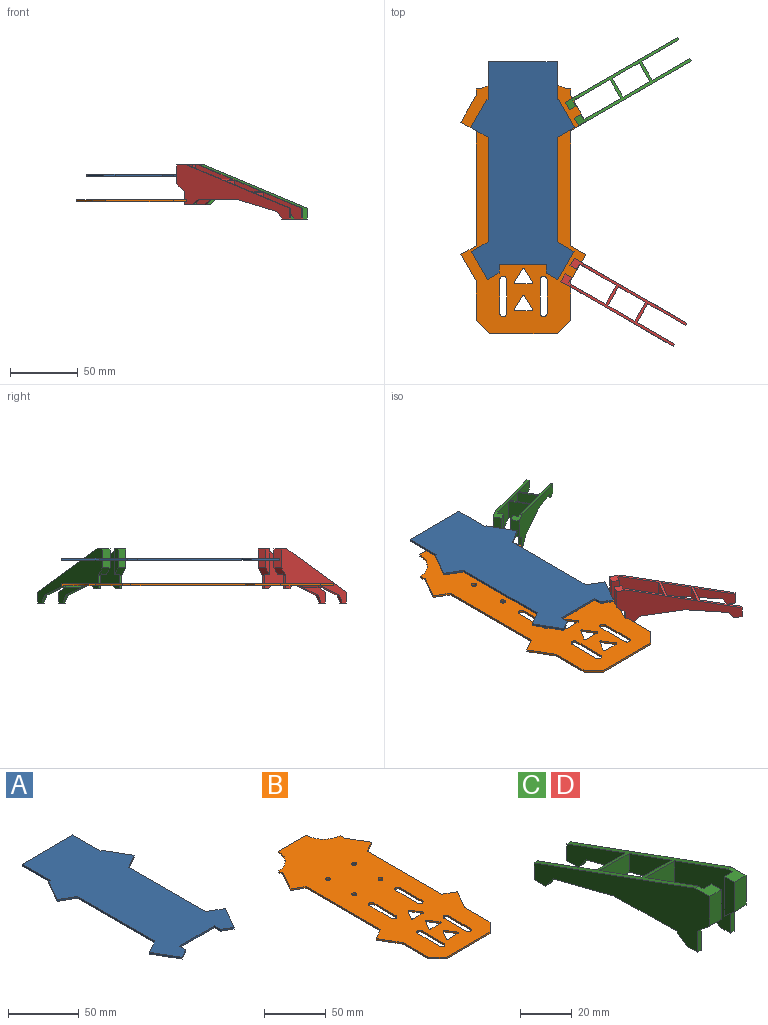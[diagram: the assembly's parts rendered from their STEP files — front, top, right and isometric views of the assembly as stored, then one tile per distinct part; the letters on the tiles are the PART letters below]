
ASSEMBLY  parts=4 mates=2
PART A: 22 faces, bbox 77x161.1x1.5 mm
  f0: plane 77.29x1.5mm, normal (-1,0,0), area 115.9mm2, adj f1,f19,f20,f21
  f1: plane 12.5x7.22mm, normal (-0.5,0.87,0), area 21.7mm2, adj f0,f2,f20,f21
  f2: plane 20.78x12mm, normal (-0.87,-0.5,0), area 36mm2, adj f1,f3,f20,f21
  f3: plane 8.5x4.91mm, normal (0.5,-0.87,0), area 14.7mm2, adj f2,f4,f20,f21
  f4: plane 6.24x1.5mm, normal (1,0,0), area 9.4mm2, adj f3,f5,f20,f21
  f5: plane 35x1.5mm, normal (0,-1,0), area 52.5mm2, adj f4,f6,f20,f21
  f6: plane 6.24x1.5mm, normal (-1,0,0), area 9.4mm2, adj f5,f7,f20,f21
  f7: plane 8.5x4.91mm, normal (-0.5,-0.87,0), area 14.7mm2, adj f6,f8,f20,f21
  f8: plane 20.78x12mm, normal (0.87,-0.5,0), area 36mm2, adj f7,f9,f20,f21
  f9: plane 12.5x7.22mm, normal (0.5,0.87,0), area 21.7mm2, adj f8,f10,f20,f21
  f10: plane 77.29x1.5mm, normal (1,0,0), area 115.9mm2, adj f9,f11,f20,f21
  f11: plane 13x7.51mm, normal (0.5,-0.87,0), area 22.5mm2, adj f10,f12,f20,f21
  f12: plane 20.78x12mm, normal (0.87,0.5,0), area 36mm2, adj f11,f13,f20,f21
  f13: plane 1.5x1mm, normal (-0.5,0.87,0), area 1.7mm2, adj f12,f14,f20,f21
  f14: plane 28.14x1.5mm, normal (1,0,0), area 42.2mm2, adj f13,f15,f20,f21
  f15: plane 51x1.5mm, normal (0,1,0), area 76.5mm2, adj f14,f16,f20,f21
  f16: plane 28.14x1.5mm, normal (-1,0,0), area 42.2mm2, adj f15,f17,f20,f21
  f17: plane 1.5x1mm, normal (0.5,0.87,0), area 1.7mm2, adj f16,f18,f20,f21
  f18: plane 20.78x12mm, normal (-0.87,0.5,0), area 36mm2, adj f17,f19,f20,f21
  f19: plane 13x7.51mm, normal (-0.5,-0.87,0), area 22.5mm2, adj f0,f18,f20,f21
  f20: plane 161.15x77mm, normal (0,0,1), area 8535mm2, adj f0,f1,f2,f3,f4,f5,f6,f7
  f21: plane 161.15x77mm, normal (0,0,-1), area 8535mm2, adj f0,f1,f2,f3,f4,f5,f6,f7
PART B: 60 faces, bbox 92.5x201x1.5 mm
  f0: plane 29.03x1.5mm, normal (1,0,0), area 43.5mm2, adj f5,f6,f7,f37
  f1: plane 29.03x1.5mm, normal (-1,0,0), area 43.5mm2, adj f5,f6,f17,f18
  f2: plane 50x1.5mm, normal (0,-1,0), area 75mm2, adj f5,f6,f18,f37
  f3: plane 5.06x1.5mm, normal (1,0,0), area 7.6mm2, adj f5,f6,f11,f59
  f4: plane 32x1.5mm, normal (0,1,0), area 48mm2, adj f5,f6,f58,f59
  f5: plane 201x92.5mm, normal (0,0,1), area 13073.6mm2, adj f0,f1,f2,f3,f4,f7,f8,f9
  f6: plane 201x92.5mm, normal (0,0,-1), area 13073.6mm2, adj f0,f1,f2,f3,f4,f7,f8,f9
  f7: plane 19.49x11.25mm, normal (0.87,-0.5,0), area 33.7mm2, adj f0,f5,f6,f8
  f8: plane 11.25x6.5mm, normal (0.5,0.87,0), area 19.5mm2, adj f5,f6,f7,f9
  f9: plane 84.98x1.5mm, normal (1,0,0), area 127.5mm2, adj f5,f6,f8,f10
  f10: plane 11.25x6.5mm, normal (0.5,-0.87,0), area 19.5mm2, adj f5,f6,f9,f11
  f11: plane 19.49x11.25mm, normal (0.87,0.5,0), area 33.7mm2, adj f3,f5,f6,f10
  f12: plane 5.06x1.5mm, normal (-1,0,0), area 7.6mm2, adj f5,f6,f13,f58
  f13: plane 19.49x11.25mm, normal (-0.87,0.5,0), area 33.7mm2, adj f5,f6,f12,f14
  f14: plane 11.25x6.5mm, normal (-0.5,-0.87,0), area 19.5mm2, adj f5,f6,f13,f15
  f15: plane 84.98x1.5mm, normal (-1,0,0), area 127.5mm2, adj f5,f6,f14,f16
  f16: plane 11.25x6.5mm, normal (-0.5,0.87,0), area 19.5mm2, adj f5,f6,f15,f17
  f17: plane 19.49x11.25mm, normal (-0.87,-0.5,0), area 33.7mm2, adj f1,f5,f6,f16
  f18: plane 10x10mm, normal (-0.71,-0.71,0), area 21.2mm2, adj f1,f2,f5,f6
  f19: plane 9.11x5.7mm, normal (-0.85,-0.53,0), area 16.1mm2, adj f5,f6,f20,f24
  f20: cylinder r=1mm len=1.7mm, axis (0,0,1), area 3mm2, adj f5,f6,f19,f21
  f21: plane 9.11x5.7mm, normal (0.85,-0.53,0), area 16.1mm2, adj f5,f6,f20,f22
  f22: cylinder r=1mm len=1.53mm, axis (0,0,1), area 3.2mm2, adj f5,f6,f21,f23
  f23: plane 11.39x1.5mm, normal (0,1,0), area 17.1mm2, adj f5,f6,f22,f24
  f24: cylinder r=1mm len=1.53mm, axis (0,0,1), area 3.2mm2, adj f5,f6,f19,f23
  f25: plane 9.11x5.7mm, normal (-0.85,-0.53,0), area 16.1mm2, adj f5,f6,f26,f30
  f26: cylinder r=1mm len=1.7mm, axis (0,0,1), area 3mm2, adj f5,f6,f25,f27
  f27: plane 9.11x5.7mm, normal (0.85,-0.53,0), area 16.1mm2, adj f5,f6,f26,f28
  f28: cylinder r=1mm len=1.53mm, axis (0,0,1), area 3.2mm2, adj f5,f6,f27,f29
  f29: plane 11.39x1.5mm, normal (0,1,0), area 17.1mm2, adj f5,f6,f28,f30
  f30: cylinder r=1mm len=1.53mm, axis (0,0,1), area 3.2mm2, adj f5,f6,f25,f29
  f31: plane 9.11x5.7mm, normal (-0.85,-0.53,0), area 16.1mm2, adj f5,f6,f32,f36
  f32: cylinder r=1mm len=1.7mm, axis (0,0,1), area 3mm2, adj f5,f6,f31,f33
  f33: plane 9.11x5.7mm, normal (0.85,-0.53,0), area 16.1mm2, adj f5,f6,f32,f34
  f34: cylinder r=1mm len=1.53mm, axis (0,0,1), area 3.2mm2, adj f5,f6,f33,f35
  f35: plane 11.39x1.5mm, normal (0,1,0), area 17.1mm2, adj f5,f6,f34,f36
  f36: cylinder r=1mm len=1.53mm, axis (0,0,1), area 3.2mm2, adj f5,f6,f31,f35
  f37: plane 10x10mm, normal (0.71,-0.71,0), area 21.2mm2, adj f0,f2,f5,f6
  f38: cylinder r=2.5mm len=5mm, axis (0,0,1), area 11.8mm2, adj f5,f6,f39,f41
  f39: plane 25x1.5mm, normal (1,0,0), area 37.5mm2, adj f5,f6,f38,f40
  f40: cylinder r=2.5mm len=5mm, axis (0,0,1), area 11.8mm2, adj f5,f6,f39,f41
  f41: plane 25x1.5mm, normal (-1,0,0), area 37.5mm2, adj f5,f6,f38,f40
  f42: cylinder r=2.5mm len=5mm, axis (0,0,1), area 11.8mm2, adj f5,f6,f43,f45
  f43: plane 25x1.5mm, normal (-1,0,0), area 37.5mm2, adj f5,f6,f42,f44
  f44: cylinder r=2.5mm len=5mm, axis (0,0,1), area 11.8mm2, adj f5,f6,f43,f45
  f45: plane 25x1.5mm, normal (1,0,0), area 37.5mm2, adj f5,f6,f42,f44
  f46: cylinder r=2.5mm len=5mm, axis (0,0,1), area 11.8mm2, adj f5,f6,f47,f49
  f47: plane 25x1.5mm, normal (1,0,0), area 37.5mm2, adj f5,f6,f46,f48
  f48: cylinder r=2.5mm len=5mm, axis (0,0,1), area 11.8mm2, adj f5,f6,f47,f49
  f49: plane 25x1.5mm, normal (-1,0,0), area 37.5mm2, adj f5,f6,f46,f48
  f50: plane 25x1.5mm, normal (-1,0,0), area 37.5mm2, adj f5,f6,f51,f53
  f51: cylinder r=2.5mm len=5mm, axis (0,0,1), area 11.8mm2, adj f5,f6,f50,f52
  f52: plane 25x1.5mm, normal (1,0,0), area 37.5mm2, adj f5,f6,f51,f53
  f53: cylinder r=2.5mm len=5mm, axis (0,0,1), area 11.8mm2, adj f5,f6,f50,f52
  f54: cylinder r=2mm len=4mm, axis (0,0,1), area 18.8mm2, adj f5,f6
  f55: cylinder r=2mm len=4mm, axis (0,0,1), area 18.8mm2, adj f5,f6
  f56: cylinder r=2mm len=4mm, axis (0,0,1), area 18.8mm2, adj f5,f6
  f57: cylinder r=2mm len=4mm, axis (0,0,1), area 18.8mm2, adj f5,f6
  f58: cylinder r=20mm len=19.98mm, axis (0,0,1), area 45.6mm2, adj f4,f5,f6,f12
  f59: cylinder r=20mm len=19.98mm, axis (0,0,1), area 45.6mm2, adj f3,f4,f5,f6
PART C: 37 faces, bbox 20x96x40 mm
  f0: plane 7.97x2mm, normal (0,1,0), area 15.9mm2, adj f1,f2,f19,f20
  f1: plane 32x19.62mm, normal (1,0,0), area 249.2mm2, adj f0,f8,f19,f20,f30,f31
  f2: plane 96x40mm, normal (-1,0,0), area 1314.7mm2, adj f0,f10,f12,f19,f20,f21,f23,f25
  f3: plane 31.5x29.6mm, normal (1,0,0), area 678.9mm2, adj f4,f10,f14,f20,f21,f23,f25,f27
  f4: plane 16x15.07mm, normal (0,-1,0), area 241.1mm2, adj f3,f5,f20,f29
  f5: plane 31.5x29.6mm, normal (-1,0,0), area 678.9mm2, adj f4,f9,f15,f20,f22,f24,f26,f28
  f6: plane 96x40mm, normal (1,0,0), area 1314.7mm2, adj f9,f11,f17,f18,f20,f22,f24,f26
  f7: plane 32x19.62mm, normal (-1,0,0), area 249.2mm2, adj f8,f11,f18,f20,f30,f32
  f8: plane 16x8.49mm, normal (0,1,0), area 135.8mm2, adj f1,f7,f20,f30
  f9: plane 8x6.5mm, normal (0,0,1), area 40.7mm2, adj f5,f6,f15,f16,f17,f20
  f10: plane 8x6.5mm, normal (0,0,1), area 40.7mm2, adj f2,f3,f12,f13,f14,f20
  f11: plane 6.2x2mm, normal (0,0,-1), area 12.4mm2, adj f6,f7,f18,f32
  f12: plane 14x6.5mm, normal (0,-1,0), area 91mm2, adj f2,f10,f13,f21
  f13: plane 18.74x5.5mm, normal (1,0,0), area 90mm2, adj f10,f12,f14,f21
  f14: plane 18.74x4.5mm, normal (0,1,0), area 84.3mm2, adj f3,f10,f13,f21
  f15: plane 18.74x4.5mm, normal (0,1,0), area 84.3mm2, adj f5,f9,f16,f22
  f16: plane 18.74x5.5mm, normal (-1,0,0), area 90mm2, adj f9,f15,f17,f22
  f17: plane 14x6.5mm, normal (0,-1,0), area 91mm2, adj f6,f9,f16,f22
  f18: plane 7.97x2mm, normal (0,1,0), area 15.9mm2, adj f6,f7,f11,f20
  f19: plane 6.2x2mm, normal (0,0,-1), area 12.4mm2, adj f0,f1,f2,f31
  f20: plane 88x32.03mm, normal (0,0.34,0.94), area 442.7mm2, adj f0,f1,f2,f3,f4,f5,f6,f7
  f21: plane 6.5x6.5mm, normal (0,-0.65,-0.76), area 49.8mm2, adj f2,f3,f12,f13,f14,f23
  f22: plane 6.5x6.5mm, normal (0,-0.65,-0.76), area 49.8mm2, adj f5,f6,f15,f16,f17,f24
  f23: plane 10x2mm, normal (0,-1,0), area 20mm2, adj f2,f3,f21,f25
  f24: plane 10x2mm, normal (0,-1,0), area 20mm2, adj f5,f6,f22,f26
  f25: plane 6x2mm, normal (0,0,-1), area 12mm2, adj f2,f3,f23,f27
  f26: plane 6x2mm, normal (0,0,-1), area 12mm2, adj f5,f6,f24,f28
  f27: plane 5.62x4.29mm, normal (0,0.61,-0.8), area 14.1mm2, adj f2,f3,f25,f29
  f28: plane 5.62x4.29mm, normal (0,0.61,-0.8), area 14.1mm2, adj f5,f6,f26,f29
  f29: plane 34.23x20mm, normal (0,-0.02,-1), area 168.9mm2, adj f2,f3,f4,f5,f6,f27,f28,f30
  f30: plane 33.16x20mm, normal (0,-0.25,-0.97), area 170mm2, adj f1,f2,f6,f7,f8,f29,f31,f32
  f31: plane 5.62x4.29mm, normal (0,-0.8,-0.61), area 14.1mm2, adj f1,f2,f19,f30
  f32: plane 5.62x4.29mm, normal (0,-0.8,-0.61), area 14.1mm2, adj f6,f7,f11,f30
  f33: plane 23x17.07mm, normal (-1,0,0), area 250mm2, adj f20,f29,f30,f34,f36
  f34: plane 16x8.7mm, normal (0,-1,0), area 139.2mm2, adj f20,f30,f33,f35
  f35: plane 23x17.07mm, normal (1,0,0), area 250mm2, adj f20,f29,f30,f34,f36
  f36: plane 16x14.38mm, normal (0,1,0), area 230mm2, adj f20,f29,f33,f35
PART D: same geometry as C
PLACE A t=(-11.67,40.84,52.02)mm
PLACE B t=(-11.12,15.34,33.32)mm
PLACE C rot(axis=(0,0,-1),60deg) t=(63.75,99.75,20.45)mm
PLACE D rot(axis=(0,0,-1),120deg) t=(60.52,-60.42,20.46)mm
MATE planar A.f15 <-> B.f4  axis (0,1,0) through (-11.67,115.84,52.77)mm
MATE planar D.f6 <-> A.f7  axis (-0.5,-0.87,0) through (48.21,-64.86,41.5)mm
